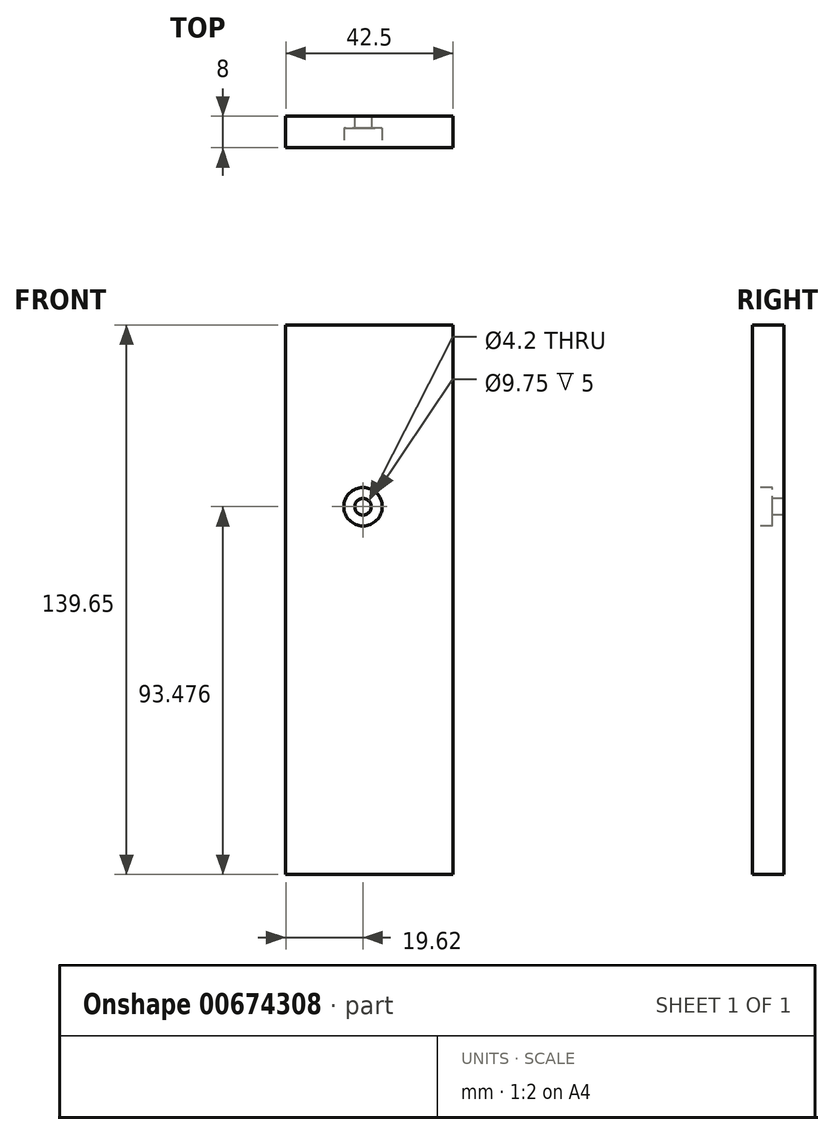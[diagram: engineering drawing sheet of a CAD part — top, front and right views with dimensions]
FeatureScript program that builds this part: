
annotation { "Feature Type Name" : "Feature", "Feature Type Description" : "" }
export const myFeature = defineFeature(function(context is Context, id is Id, definition is map)
    precondition{}
    {
        {
            var Q0;
            Q0=qCreatedBy(makeId("Front.planeOp"),FACE);
            var sketch = newSketch(context, id + "F0", { "sketchPlane" : qUnion([Q0])});
            skLineSegment(sketch, "E0.bottom", {"start": v(-19.62, 95.28) * mm, "end": v(22.88, 95.28) * mm});
            skLineSegment(sketch, "E0.top", {"start": v(-19.62, -44.37) * mm, "end": v(22.88, -44.37) * mm});
            skLineSegment(sketch, "E0.left", {"start": v(-19.62, 95.28) * mm, "end": v(-19.62, -44.37) * mm});
            skLineSegment(sketch, "E0.right", {"start": v(22.88, 95.28) * mm, "end": v(22.88, -44.37) * mm});
            skSolve(sketch);
        }
        {
            var Q0;
            Q0 = qSketchRegion(id + "F0", true);
            extrude(context, id + "F1", {"entities" : qUnion([Q0]), "depth" : 8 * mm, "offsetDistance" : 25 * mm});
        }
        {
            var Q0;
            Q0=makeQuery(id+"F1.opExtrude","CAP_FACE",FACE,{"disambiguationData":[OSD([sQuery(id+"F0.wireOp",EDGE,"E0.bottom"),sQuery(id+"F0.wireOp",EDGE,"E0.top"),sQuery(id+"F0.wireOp",EDGE,"E0.left"),sQuery(id+"F0.wireOp",EDGE,"E0.right")])],"isStart":false});
            var sketch = newSketch(context, id + "F2", { "sketchPlane" : qUnion([Q0])});
            skPoint(sketch, "E1", {"position": v(0, 49.1) * mm});
            skSolve(sketch);
        }
        {
            var Q0;
            Q0=sQuery(id+"F2.wireOp",VERTEX,"E1");
            var Q1;
            Q1=makeQuery(id+"F1.opExtrude","SWEPT_BODY",BODY,{"disambiguationData":[OSD([sQuery(id+"F0.wireOp",EDGE,"E0.bottom"),sQuery(id+"F0.wireOp",EDGE,"E0.top"),sQuery(id+"F0.wireOp",EDGE,"E0.left"),sQuery(id+"F0.wireOp",EDGE,"E0.right")])]});
            hole(context, id + "F3", {"style" : HoleStyle.C_BORE, "endStyle" : HoleEndStyle.BLIND, "holeDiameter" : 4.2 * mm, "cBoreDiameter" : 9.75 * mm, "cBoreDepth" : 5 * mm, "majorDiameter" : 5 * mm, "holeDepth" : 14.4 * mm, "isTappedThrough" : true, "tappedDepth" : 12 * mm, "tapClearance" : 3, "startFromSketch" : true, "locations" : qUnion([Q0]), "scope" : qUnion([Q1])});
        }
    });
